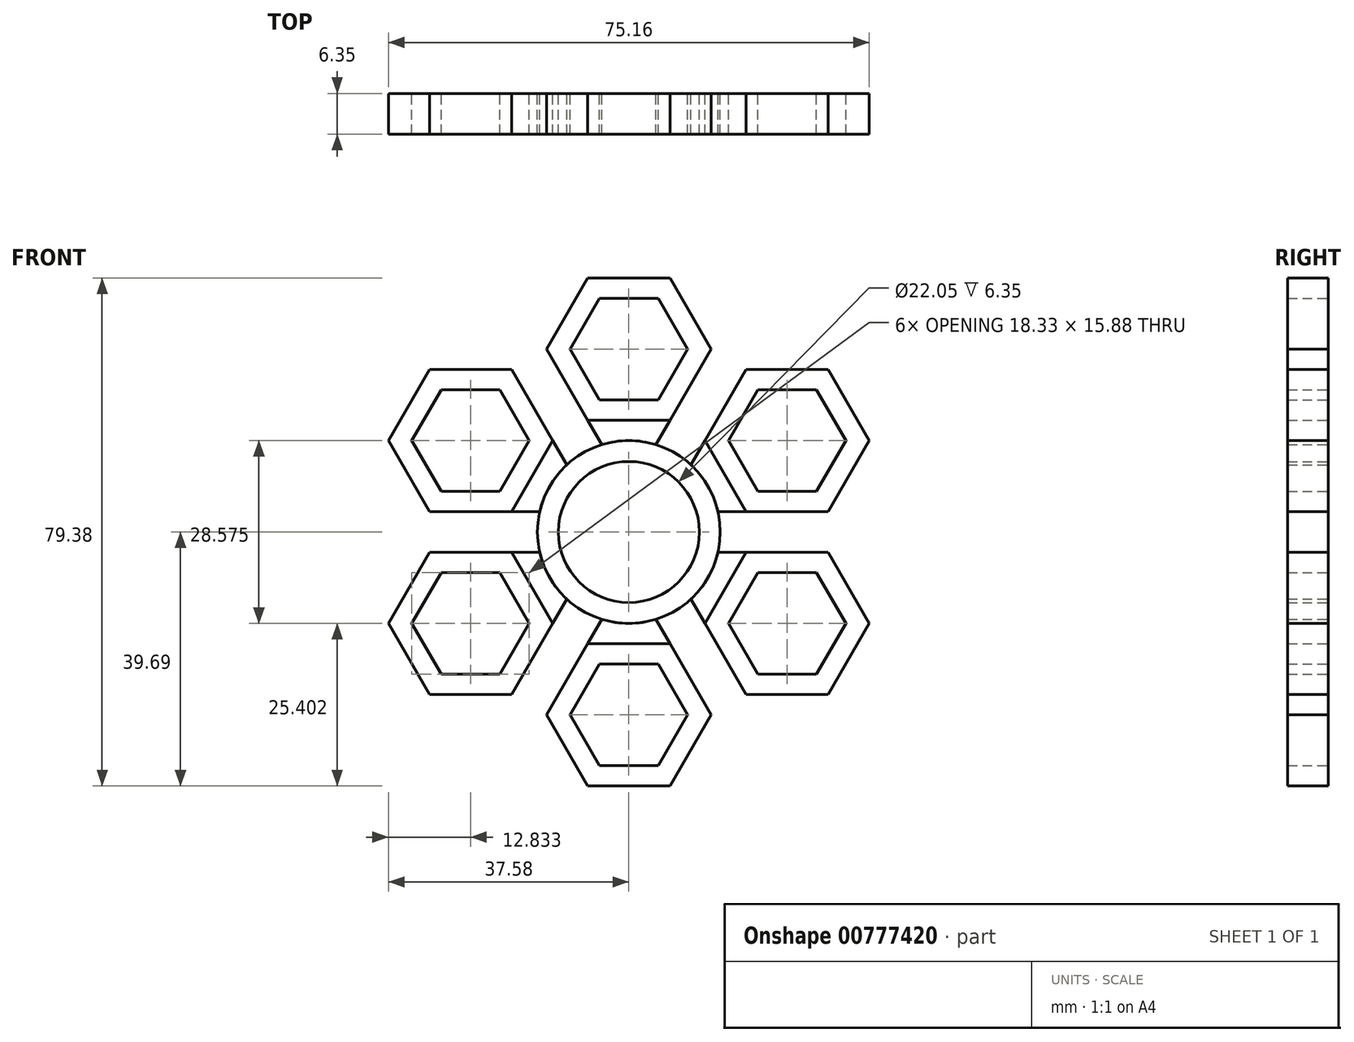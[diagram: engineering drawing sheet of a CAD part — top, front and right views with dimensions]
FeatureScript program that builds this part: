
annotation { "Feature Type Name" : "Feature", "Feature Type Description" : "" }
export const myFeature = defineFeature(function(context is Context, id is Id, definition is map)
    precondition{}
    {
        {
            var Q0;
            Q0=qCreatedBy(makeId("Front.planeOp"),FACE);
            var sketch = newSketch(context, id + "F0", { "sketchPlane" : qUnion([Q0])});
            skCircle(sketch, "E0", {"center": v(0, 0) * mm, "radius": 11.02 * mm});
            skCircle(sketch, "E1", {"center": v(0, 0) * mm, "radius": 14.29 * mm});
            skCircle(sketch, "E2.cCircle", {"center": v(0, 28.58) * mm, "radius": 7.94 * mm, "construction": true});
            skLineSegment(sketch, "E2.0", {"start": v(4.58, 20.64) * mm, "end": v(-4.58, 20.64) * mm});
            skLineSegment(sketch, "E2.1", {"start": v(-4.58, 20.64) * mm, "end": v(-9.17, 28.57) * mm});
            skLineSegment(sketch, "E2.2", {"start": v(-9.17, 28.57) * mm, "end": v(-4.58, 36.51) * mm});
            skLineSegment(sketch, "E2.3", {"start": v(-4.58, 36.51) * mm, "end": v(4.58, 36.51) * mm});
            skLineSegment(sketch, "E2.4", {"start": v(4.58, 36.51) * mm, "end": v(9.17, 28.58) * mm});
            skLineSegment(sketch, "E2.5", {"start": v(9.17, 28.58) * mm, "end": v(4.58, 20.64) * mm});
            skPoint(sketch, "E2.0.midPoint", {"position": v(0, 20.64) * mm});
            skCircle(sketch, "E3.cCircle", {"center": v(0, 28.58) * mm, "radius": 11.11 * mm, "construction": true});
            skLineSegment(sketch, "E3.0", {"start": v(6.42, 17.46) * mm, "end": v(-6.42, 17.46) * mm});
            skLineSegment(sketch, "E3.1", {"start": v(-6.42, 17.46) * mm, "end": v(-12.83, 28.57) * mm});
            skLineSegment(sketch, "E3.2", {"start": v(-12.83, 28.57) * mm, "end": v(-6.42, 39.69) * mm});
            skLineSegment(sketch, "E3.3", {"start": v(-6.42, 39.69) * mm, "end": v(6.42, 39.69) * mm});
            skLineSegment(sketch, "E3.4", {"start": v(6.42, 39.69) * mm, "end": v(12.83, 28.58) * mm});
            skLineSegment(sketch, "E3.5", {"start": v(12.83, 28.57) * mm, "end": v(6.42, 17.46) * mm});
            skPoint(sketch, "E3.0.midPoint", {"position": v(0, 17.46) * mm});
            skCircle(sketch, "E4.1.0", {"center": v(-24.75, 14.29) * mm, "radius": 7.94 * mm, "construction": true});
            skLineSegment(sketch, "E4.1.1", {"start": v(-15.58, 14.29) * mm, "end": v(-20.16, 6.35) * mm});
            skPoint(sketch, "E4.1.2", {"position": v(-15.12, 8.73) * mm});
            skLineSegment(sketch, "E4.1.3", {"start": v(-29.33, 6.35) * mm, "end": v(-33.91, 14.29) * mm});
            skLineSegment(sketch, "E4.1.4", {"start": v(-18.33, 25.4) * mm, "end": v(-11.92, 14.29) * mm});
            skLineSegment(sketch, "E4.1.5", {"start": v(-31.16, 25.4) * mm, "end": v(-18.33, 25.4) * mm});
            skLineSegment(sketch, "E4.1.6", {"start": v(-37.58, 14.29) * mm, "end": v(-31.16, 25.4) * mm});
            skLineSegment(sketch, "E4.1.7", {"start": v(-20.16, 6.35) * mm, "end": v(-29.33, 6.35) * mm});
            skLineSegment(sketch, "E4.1.8", {"start": v(-33.91, 14.29) * mm, "end": v(-29.33, 22.23) * mm});
            skLineSegment(sketch, "E4.1.9", {"start": v(-29.33, 22.23) * mm, "end": v(-20.16, 22.23) * mm});
            skLineSegment(sketch, "E4.1.10", {"start": v(-20.16, 22.23) * mm, "end": v(-15.58, 14.29) * mm});
            skCircle(sketch, "E4.1.11", {"center": v(-24.75, 14.29) * mm, "radius": 11.11 * mm, "construction": true});
            skLineSegment(sketch, "E4.1.12", {"start": v(-11.92, 14.29) * mm, "end": v(-18.33, 3.17) * mm});
            skLineSegment(sketch, "E4.1.13", {"start": v(-18.33, 3.17) * mm, "end": v(-31.16, 3.17) * mm});
            skLineSegment(sketch, "E4.1.14", {"start": v(-31.16, 3.17) * mm, "end": v(-37.58, 14.29) * mm});
            skPoint(sketch, "E4.1.15", {"position": v(-17.87, 10.32) * mm});
            skCircle(sketch, "E4.2.0", {"center": v(-24.75, -14.29) * mm, "radius": 7.94 * mm, "construction": true});
            skLineSegment(sketch, "E4.2.1", {"start": v(-20.16, -6.35) * mm, "end": v(-15.58, -14.29) * mm});
            skPoint(sketch, "E4.2.2", {"position": v(-15.12, -8.73) * mm});
            skLineSegment(sketch, "E4.2.3", {"start": v(-20.16, -22.22) * mm, "end": v(-29.33, -22.22) * mm});
            skLineSegment(sketch, "E4.2.4", {"start": v(-31.16, -3.17) * mm, "end": v(-18.33, -3.17) * mm});
            skLineSegment(sketch, "E4.2.5", {"start": v(-37.58, -14.29) * mm, "end": v(-31.16, -3.17) * mm});
            skLineSegment(sketch, "E4.2.6", {"start": v(-31.16, -25.4) * mm, "end": v(-37.58, -14.29) * mm});
            skLineSegment(sketch, "E4.2.7", {"start": v(-15.58, -14.29) * mm, "end": v(-20.16, -22.22) * mm});
            skLineSegment(sketch, "E4.2.8", {"start": v(-29.33, -22.22) * mm, "end": v(-33.91, -14.29) * mm});
            skLineSegment(sketch, "E4.2.9", {"start": v(-33.91, -14.29) * mm, "end": v(-29.33, -6.35) * mm});
            skLineSegment(sketch, "E4.2.10", {"start": v(-29.33, -6.35) * mm, "end": v(-20.16, -6.35) * mm});
            skCircle(sketch, "E4.2.11", {"center": v(-24.75, -14.29) * mm, "radius": 11.11 * mm, "construction": true});
            skLineSegment(sketch, "E4.2.12", {"start": v(-18.33, -3.17) * mm, "end": v(-11.92, -14.29) * mm});
            skLineSegment(sketch, "E4.2.13", {"start": v(-11.92, -14.29) * mm, "end": v(-18.33, -25.4) * mm});
            skLineSegment(sketch, "E4.2.14", {"start": v(-18.33, -25.4) * mm, "end": v(-31.16, -25.4) * mm});
            skPoint(sketch, "E4.2.15", {"position": v(-17.87, -10.32) * mm});
            skCircle(sketch, "E4.3.0", {"center": v(0, -28.58) * mm, "radius": 7.94 * mm, "construction": true});
            skLineSegment(sketch, "E4.3.1", {"start": v(-4.58, -20.64) * mm, "end": v(4.58, -20.64) * mm});
            skPoint(sketch, "E4.3.2", {"position": v(0, -17.46) * mm});
            skLineSegment(sketch, "E4.3.3", {"start": v(9.17, -28.57) * mm, "end": v(4.58, -36.51) * mm});
            skLineSegment(sketch, "E4.3.4", {"start": v(-12.83, -28.58) * mm, "end": v(-6.42, -17.46) * mm});
            skLineSegment(sketch, "E4.3.5", {"start": v(-6.42, -39.69) * mm, "end": v(-12.83, -28.58) * mm});
            skLineSegment(sketch, "E4.3.6", {"start": v(6.42, -39.69) * mm, "end": v(-6.42, -39.69) * mm});
            skLineSegment(sketch, "E4.3.7", {"start": v(4.58, -20.64) * mm, "end": v(9.17, -28.57) * mm});
            skLineSegment(sketch, "E4.3.8", {"start": v(4.58, -36.51) * mm, "end": v(-4.58, -36.51) * mm});
            skLineSegment(sketch, "E4.3.9", {"start": v(-4.58, -36.51) * mm, "end": v(-9.17, -28.58) * mm});
            skLineSegment(sketch, "E4.3.10", {"start": v(-9.17, -28.58) * mm, "end": v(-4.58, -20.64) * mm});
            skCircle(sketch, "E4.3.11", {"center": v(0, -28.58) * mm, "radius": 11.11 * mm, "construction": true});
            skLineSegment(sketch, "E4.3.12", {"start": v(-6.42, -17.46) * mm, "end": v(6.42, -17.46) * mm});
            skLineSegment(sketch, "E4.3.13", {"start": v(6.42, -17.46) * mm, "end": v(12.83, -28.57) * mm});
            skLineSegment(sketch, "E4.3.14", {"start": v(12.83, -28.57) * mm, "end": v(6.42, -39.69) * mm});
            skPoint(sketch, "E4.3.15", {"position": v(0, -20.64) * mm});
            skCircle(sketch, "E4.4.0", {"center": v(24.75, -14.29) * mm, "radius": 7.94 * mm, "construction": true});
            skLineSegment(sketch, "E4.4.1", {"start": v(15.58, -14.29) * mm, "end": v(20.16, -6.35) * mm});
            skPoint(sketch, "E4.4.2", {"position": v(15.12, -8.73) * mm});
            skLineSegment(sketch, "E4.4.3", {"start": v(29.33, -6.35) * mm, "end": v(33.91, -14.29) * mm});
            skLineSegment(sketch, "E4.4.4", {"start": v(18.33, -25.4) * mm, "end": v(11.92, -14.29) * mm});
            skLineSegment(sketch, "E4.4.5", {"start": v(31.16, -25.4) * mm, "end": v(18.33, -25.4) * mm});
            skLineSegment(sketch, "E4.4.6", {"start": v(37.58, -14.29) * mm, "end": v(31.16, -25.4) * mm});
            skLineSegment(sketch, "E4.4.7", {"start": v(20.16, -6.35) * mm, "end": v(29.33, -6.35) * mm});
            skLineSegment(sketch, "E4.4.8", {"start": v(33.91, -14.29) * mm, "end": v(29.33, -22.23) * mm});
            skLineSegment(sketch, "E4.4.9", {"start": v(29.33, -22.23) * mm, "end": v(20.16, -22.23) * mm});
            skLineSegment(sketch, "E4.4.10", {"start": v(20.16, -22.23) * mm, "end": v(15.58, -14.29) * mm});
            skCircle(sketch, "E4.4.11", {"center": v(24.75, -14.29) * mm, "radius": 11.11 * mm, "construction": true});
            skLineSegment(sketch, "E4.4.12", {"start": v(11.92, -14.29) * mm, "end": v(18.33, -3.18) * mm});
            skLineSegment(sketch, "E4.4.13", {"start": v(18.33, -3.18) * mm, "end": v(31.16, -3.17) * mm});
            skLineSegment(sketch, "E4.4.14", {"start": v(31.16, -3.18) * mm, "end": v(37.58, -14.29) * mm});
            skPoint(sketch, "E4.4.15", {"position": v(17.87, -10.32) * mm});
            skCircle(sketch, "E4.5.0", {"center": v(24.75, 14.29) * mm, "radius": 7.94 * mm, "construction": true});
            skLineSegment(sketch, "E4.5.1", {"start": v(20.16, 6.35) * mm, "end": v(15.58, 14.29) * mm});
            skPoint(sketch, "E4.5.2", {"position": v(15.12, 8.73) * mm});
            skLineSegment(sketch, "E4.5.3", {"start": v(20.16, 22.23) * mm, "end": v(29.33, 22.23) * mm});
            skLineSegment(sketch, "E4.5.4", {"start": v(31.16, 3.17) * mm, "end": v(18.33, 3.17) * mm});
            skLineSegment(sketch, "E4.5.5", {"start": v(37.58, 14.29) * mm, "end": v(31.16, 3.17) * mm});
            skLineSegment(sketch, "E4.5.6", {"start": v(31.16, 25.4) * mm, "end": v(37.58, 14.29) * mm});
            skLineSegment(sketch, "E4.5.7", {"start": v(15.58, 14.29) * mm, "end": v(20.16, 22.22) * mm});
            skLineSegment(sketch, "E4.5.8", {"start": v(29.33, 22.22) * mm, "end": v(33.91, 14.29) * mm});
            skLineSegment(sketch, "E4.5.9", {"start": v(33.91, 14.29) * mm, "end": v(29.33, 6.35) * mm});
            skLineSegment(sketch, "E4.5.10", {"start": v(29.33, 6.35) * mm, "end": v(20.16, 6.35) * mm});
            skCircle(sketch, "E4.5.11", {"center": v(24.75, 14.29) * mm, "radius": 11.11 * mm, "construction": true});
            skLineSegment(sketch, "E4.5.12", {"start": v(18.33, 3.17) * mm, "end": v(11.92, 14.29) * mm});
            skLineSegment(sketch, "E4.5.13", {"start": v(11.92, 14.29) * mm, "end": v(18.33, 25.4) * mm});
            skLineSegment(sketch, "E4.5.14", {"start": v(18.33, 25.4) * mm, "end": v(31.16, 25.4) * mm});
            skPoint(sketch, "E4.5.15", {"position": v(17.87, 10.32) * mm});
            skSolve(sketch);
        }
        {
            var Q0;
            Q0=qCreatedBy(makeId("Front.planeOp"),FACE);
            var sketch = newSketch(context, id + "F1", { "sketchPlane" : qUnion([Q0])});
            skLineSegment(sketch, "E5.0", {"start": v(15.58, -14.29) * mm, "end": v(20.16, -6.35) * mm});
            skLineSegment(sketch, "E5.1", {"start": v(-18.33, -25.4) * mm, "end": v(-31.16, -25.4) * mm});
            skLineSegment(sketch, "E5.2", {"start": v(-31.16, -25.4) * mm, "end": v(-37.58, -14.29) * mm});
            skLineSegment(sketch, "E5.3", {"start": v(4.58, -36.51) * mm, "end": v(-4.58, -36.51) * mm});
            skLineSegment(sketch, "E5.4", {"start": v(20.16, -22.23) * mm, "end": v(15.58, -14.29) * mm});
            skLineSegment(sketch, "E5.5", {"start": v(18.33, 3.17) * mm, "end": v(11.92, 14.29) * mm});
            skLineSegment(sketch, "E5.6", {"start": v(-18.33, 25.4) * mm, "end": v(-11.92, 14.29) * mm});
            skLineSegment(sketch, "E5.7", {"start": v(20.16, 22.23) * mm, "end": v(29.33, 22.23) * mm});
            skCircle(sketch, "E5.8", {"center": v(-24.75, 14.29) * mm, "radius": 11.11 * mm});
            skLineSegment(sketch, "E5.9", {"start": v(-11.92, -14.29) * mm, "end": v(-18.33, -25.4) * mm});
            skCircle(sketch, "E5.10", {"center": v(24.75, -14.29) * mm, "radius": 7.94 * mm});
            skLineSegment(sketch, "E5.11", {"start": v(-11.92, 14.29) * mm, "end": v(-18.33, 3.17) * mm});
            skLineSegment(sketch, "E5.12", {"start": v(31.16, 3.17) * mm, "end": v(18.33, 3.17) * mm});
            skLineSegment(sketch, "E5.13", {"start": v(-31.16, 25.4) * mm, "end": v(-18.33, 25.4) * mm});
            skLineSegment(sketch, "E5.14", {"start": v(11.92, 14.29) * mm, "end": v(18.33, 25.4) * mm});
            skLineSegment(sketch, "E5.15", {"start": v(31.16, 25.4) * mm, "end": v(37.58, 14.29) * mm});
            skLineSegment(sketch, "E5.16", {"start": v(18.33, -25.4) * mm, "end": v(11.92, -14.29) * mm});
            skCircle(sketch, "E5.17", {"center": v(24.75, -14.29) * mm, "radius": 11.11 * mm});
            skLineSegment(sketch, "E5.18", {"start": v(-4.58, -20.64) * mm, "end": v(4.58, -20.64) * mm});
            skLineSegment(sketch, "E5.19", {"start": v(-4.58, -36.51) * mm, "end": v(-9.17, -28.58) * mm});
            skLineSegment(sketch, "E5.20", {"start": v(-15.58, -14.29) * mm, "end": v(-20.16, -22.22) * mm});
            skLineSegment(sketch, "E5.21", {"start": v(-31.16, 3.17) * mm, "end": v(-37.58, 14.29) * mm});
            skLineSegment(sketch, "E5.22", {"start": v(29.33, -6.35) * mm, "end": v(33.91, -14.29) * mm});
            skCircle(sketch, "E5.23", {"center": v(0, -28.58) * mm, "radius": 7.94 * mm});
            skLineSegment(sketch, "E5.24", {"start": v(-18.33, 3.17) * mm, "end": v(-31.16, 3.17) * mm});
            skLineSegment(sketch, "E5.25", {"start": v(37.58, 14.29) * mm, "end": v(31.16, 3.17) * mm});
            skLineSegment(sketch, "E5.26", {"start": v(-37.58, 14.29) * mm, "end": v(-31.16, 25.4) * mm});
            skLineSegment(sketch, "E5.27", {"start": v(15.58, 14.29) * mm, "end": v(20.16, 22.22) * mm});
            skLineSegment(sketch, "E5.28", {"start": v(18.33, 25.4) * mm, "end": v(31.16, 25.4) * mm});
            skLineSegment(sketch, "E5.29", {"start": v(11.92, -14.29) * mm, "end": v(18.33, -3.18) * mm});
            skLineSegment(sketch, "E5.30", {"start": v(31.16, -25.4) * mm, "end": v(18.33, -25.4) * mm});
            skLineSegment(sketch, "E5.31", {"start": v(-9.17, -28.58) * mm, "end": v(-4.58, -20.64) * mm});
            skLineSegment(sketch, "E5.32", {"start": v(9.17, -28.57) * mm, "end": v(4.58, -36.51) * mm});
            skCircle(sketch, "E5.33", {"center": v(-24.75, -14.29) * mm, "radius": 7.94 * mm});
            skLineSegment(sketch, "E5.34", {"start": v(-29.33, -22.22) * mm, "end": v(-33.91, -14.29) * mm});
            skLineSegment(sketch, "E5.35", {"start": v(-20.16, 6.35) * mm, "end": v(-29.33, 6.35) * mm});
            skLineSegment(sketch, "E5.36", {"start": v(29.33, 22.22) * mm, "end": v(33.91, 14.29) * mm});
            skLineSegment(sketch, "E5.37", {"start": v(37.58, -14.29) * mm, "end": v(31.16, -25.4) * mm});
            skLineSegment(sketch, "E5.38", {"start": v(18.33, -3.18) * mm, "end": v(31.16, -3.17) * mm});
            skLineSegment(sketch, "E5.39", {"start": v(-12.83, -28.58) * mm, "end": v(-6.42, -17.46) * mm});
            skCircle(sketch, "E5.40", {"center": v(0, -28.58) * mm, "radius": 11.11 * mm});
            skLineSegment(sketch, "E5.41", {"start": v(-20.16, -6.35) * mm, "end": v(-15.58, -14.29) * mm});
            skLineSegment(sketch, "E5.42", {"start": v(-33.91, -14.29) * mm, "end": v(-29.33, -6.35) * mm});
            skLineSegment(sketch, "E5.43", {"start": v(-6.42, 39.69) * mm, "end": v(6.42, 39.69) * mm});
            skLineSegment(sketch, "E5.44", {"start": v(6.42, 39.69) * mm, "end": v(12.83, 28.58) * mm});
            skLineSegment(sketch, "E5.45", {"start": v(12.83, 28.57) * mm, "end": v(6.42, 17.46) * mm});
            skCircle(sketch, "E5.46", {"center": v(0, 0) * mm, "radius": 11.02 * mm});
            skCircle(sketch, "E5.47", {"center": v(0, 0) * mm, "radius": 14.29 * mm});
            skCircle(sketch, "E5.48", {"center": v(0, 28.58) * mm, "radius": 7.94 * mm});
            skLineSegment(sketch, "E5.49", {"start": v(4.58, 20.64) * mm, "end": v(-4.58, 20.64) * mm});
            skLineSegment(sketch, "E5.50", {"start": v(-4.58, 20.64) * mm, "end": v(-9.17, 28.57) * mm});
            skLineSegment(sketch, "E5.51", {"start": v(-9.17, 28.57) * mm, "end": v(-4.58, 36.51) * mm});
            skLineSegment(sketch, "E5.52", {"start": v(-4.58, 36.51) * mm, "end": v(4.58, 36.51) * mm});
            skLineSegment(sketch, "E5.53", {"start": v(4.58, 36.51) * mm, "end": v(9.17, 28.58) * mm});
            skLineSegment(sketch, "E5.54", {"start": v(9.17, 28.58) * mm, "end": v(4.58, 20.64) * mm});
            skCircle(sketch, "E5.55", {"center": v(0, 28.58) * mm, "radius": 11.11 * mm});
            skLineSegment(sketch, "E5.56", {"start": v(6.42, 17.46) * mm, "end": v(-6.42, 17.46) * mm});
            skLineSegment(sketch, "E5.57", {"start": v(-6.42, 17.46) * mm, "end": v(-12.83, 28.57) * mm});
            skLineSegment(sketch, "E5.58", {"start": v(-12.83, 28.57) * mm, "end": v(-6.42, 39.69) * mm});
            skLineSegment(sketch, "E5.59", {"start": v(-6.42, -17.46) * mm, "end": v(6.42, -17.46) * mm});
            skLineSegment(sketch, "E5.60", {"start": v(-29.33, -6.35) * mm, "end": v(-20.16, -6.35) * mm});
            skLineSegment(sketch, "E5.61", {"start": v(-33.91, 14.29) * mm, "end": v(-29.33, 22.23) * mm});
            skLineSegment(sketch, "E5.62", {"start": v(31.16, -3.18) * mm, "end": v(37.58, -14.29) * mm});
            skCircle(sketch, "E5.63", {"center": v(-24.75, 14.29) * mm, "radius": 7.94 * mm});
            skLineSegment(sketch, "E5.64", {"start": v(33.91, 14.29) * mm, "end": v(29.33, 6.35) * mm});
            skLineSegment(sketch, "E5.65", {"start": v(20.16, -6.35) * mm, "end": v(29.33, -6.35) * mm});
            skLineSegment(sketch, "E5.66", {"start": v(-6.42, -39.69) * mm, "end": v(-12.83, -28.58) * mm});
            skLineSegment(sketch, "E5.67", {"start": v(-20.16, -22.22) * mm, "end": v(-29.33, -22.22) * mm});
            skLineSegment(sketch, "E5.68", {"start": v(6.42, -17.46) * mm, "end": v(12.83, -28.57) * mm});
            skCircle(sketch, "E5.69", {"center": v(-24.75, -14.29) * mm, "radius": 11.11 * mm});
            skLineSegment(sketch, "E5.70", {"start": v(-29.33, 22.23) * mm, "end": v(-20.16, 22.23) * mm});
            skCircle(sketch, "E5.71", {"center": v(24.75, 14.29) * mm, "radius": 7.94 * mm});
            skLineSegment(sketch, "E5.72", {"start": v(-15.58, 14.29) * mm, "end": v(-20.16, 6.35) * mm});
            skLineSegment(sketch, "E5.73", {"start": v(29.33, 6.35) * mm, "end": v(20.16, 6.35) * mm});
            skLineSegment(sketch, "E5.74", {"start": v(33.91, -14.29) * mm, "end": v(29.33, -22.23) * mm});
            skLineSegment(sketch, "E5.75", {"start": v(6.42, -39.69) * mm, "end": v(-6.42, -39.69) * mm});
            skLineSegment(sketch, "E5.76", {"start": v(-31.16, -3.17) * mm, "end": v(-18.33, -3.17) * mm});
            skLineSegment(sketch, "E5.77", {"start": v(12.83, -28.57) * mm, "end": v(6.42, -39.69) * mm});
            skLineSegment(sketch, "E5.78", {"start": v(-18.33, -3.17) * mm, "end": v(-11.92, -14.29) * mm});
            skLineSegment(sketch, "E5.79", {"start": v(-20.16, 22.23) * mm, "end": v(-15.58, 14.29) * mm});
            skLineSegment(sketch, "E5.80", {"start": v(20.16, 6.35) * mm, "end": v(15.58, 14.29) * mm});
            skLineSegment(sketch, "E5.81", {"start": v(-29.33, 6.35) * mm, "end": v(-33.91, 14.29) * mm});
            skCircle(sketch, "E5.82", {"center": v(24.75, 14.29) * mm, "radius": 11.11 * mm});
            skLineSegment(sketch, "E5.83", {"start": v(29.33, -22.23) * mm, "end": v(20.16, -22.23) * mm});
            skLineSegment(sketch, "E5.84", {"start": v(4.58, -20.64) * mm, "end": v(9.17, -28.57) * mm});
            skLineSegment(sketch, "E5.85", {"start": v(-37.58, -14.29) * mm, "end": v(-31.16, -3.17) * mm});
            skLineSegment(sketch, "E6", {"start": v(-18.33, -3.17) * mm, "end": v(-13.93, -3.17) * mm});
            skLineSegment(sketch, "E7", {"start": v(-11.92, -14.29) * mm, "end": v(-9.71, -10.48) * mm});
            skLineSegment(sketch, "E8", {"start": v(-6.42, -17.46) * mm, "end": v(-4.22, -13.65) * mm});
            skLineSegment(sketch, "E9", {"start": v(6.42, -17.46) * mm, "end": v(4.22, -13.65) * mm});
            skLineSegment(sketch, "E10", {"start": v(-18.33, 3.17) * mm, "end": v(-13.93, 3.17) * mm});
            skLineSegment(sketch, "E11", {"start": v(-11.92, 14.29) * mm, "end": v(-9.71, 10.48) * mm});
            skLineSegment(sketch, "E12", {"start": v(6.42, 17.46) * mm, "end": v(4.22, 13.65) * mm});
            skLineSegment(sketch, "E13", {"start": v(-6.42, 17.46) * mm, "end": v(-4.22, 13.65) * mm});
            skLineSegment(sketch, "E14", {"start": v(18.33, 3.17) * mm, "end": v(13.93, 3.17) * mm});
            skLineSegment(sketch, "E15", {"start": v(11.92, 14.29) * mm, "end": v(9.71, 10.48) * mm});
            skLineSegment(sketch, "E16", {"start": v(18.33, -3.18) * mm, "end": v(13.93, -3.18) * mm});
            skLineSegment(sketch, "E17", {"start": v(11.92, -14.29) * mm, "end": v(9.71, -10.48) * mm});
            skLineSegment(sketch, "E18", {"start": v(9.71, -10.48) * mm, "end": v(9.95, -10.9) * mm});
            skSolve(sketch);
        }
        {
            var Q0;
            Q0 = qSketchRegion(id + "F0", true);
            var Q1;
            {var subQ0=sQuery(id+"F1.wireOp",EDGE,"E10");Q1=makeQuery(id+"F1.imprint","IMPRINT",FACE,{"disambiguationData":[TD([[makeQuery(id+"F1.imprint","IMPRINT",EDGE,{"derivedFrom":subQ0}),1.0]])]});}
            var Q2;
            {var subQ3=sQuery(id+"F1.wireOp",EDGE,"E6");Q2=makeQuery(id+"F1.imprint","IMPRINT",FACE,{"disambiguationData":[TD([[makeQuery(id+"F1.imprint","IMPRINT",EDGE,{"derivedFrom":subQ3}),-1.0]])]});}
            var Q3;
            {var subQ0=sQuery(id+"F1.wireOp",EDGE,"E8");Q3=makeQuery(id+"F1.imprint","IMPRINT",FACE,{"disambiguationData":[TD([[makeQuery(id+"F1.imprint","IMPRINT",EDGE,{"derivedFrom":subQ0}),-1.0]])]});}
            var Q4;
            {var subQ0=sQuery(id+"F1.wireOp",EDGE,"E16");Q4=makeQuery(id+"F1.imprint","IMPRINT",FACE,{"disambiguationData":[TD([[makeQuery(id+"F1.imprint","IMPRINT",EDGE,{"derivedFrom":subQ0}),1.0]])]});}
            var Q5;
            {var subQ0=sQuery(id+"F1.wireOp",EDGE,"E14");Q5=makeQuery(id+"F1.imprint","IMPRINT",FACE,{"disambiguationData":[TD([[makeQuery(id+"F1.imprint","IMPRINT",EDGE,{"derivedFrom":subQ0}),-1.0]])]});}
            var Q6;
            {var subQ0=sQuery(id+"F1.wireOp",EDGE,"E12");Q6=makeQuery(id+"F1.imprint","IMPRINT",FACE,{"disambiguationData":[TD([[makeQuery(id+"F1.imprint","IMPRINT",EDGE,{"derivedFrom":subQ0}),-1.0]])]});}
            extrude(context, id + "F2", {"entities" : qUnion([Q0, Q1, Q2, Q3, Q4, Q5, Q6]), "depth" : 6.35 * mm, "offsetDistance" : 25.4 * mm});
        }
    });
